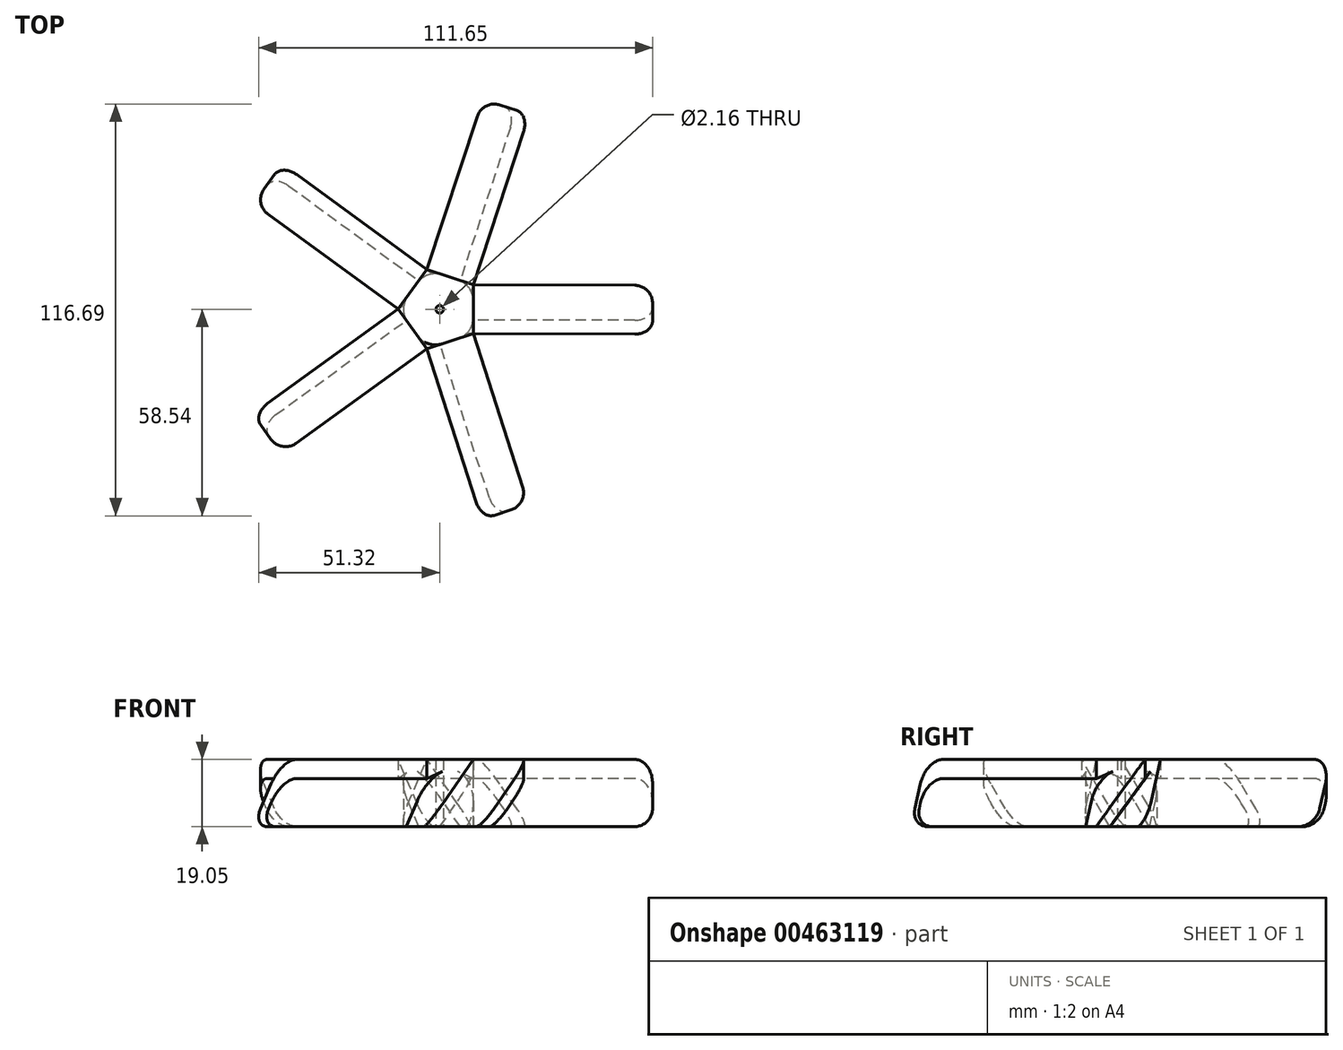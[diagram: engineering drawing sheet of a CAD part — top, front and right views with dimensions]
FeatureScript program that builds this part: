
annotation { "Feature Type Name" : "Feature", "Feature Type Description" : "" }
export const myFeature = defineFeature(function(context is Context, id is Id, definition is map)
    precondition{}
    {
        {
            var Q0;
            Q0=qCreatedBy(makeId("Top.planeOp"),FACE);
            var sketch = newSketch(context, id + "F0", { "sketchPlane" : qUnion([Q0])});
            skCircle(sketch, "E0.cCircle", {"center": v(0, 0) * mm, "radius": 9.53 * mm, "construction": true});
            skLineSegment(sketch, "E0.0", {"start": v(9.5, -6.94) * mm, "end": v(-3.67, -11.19) * mm});
            skLineSegment(sketch, "E0.1", {"start": v(-3.67, -11.19) * mm, "end": v(-11.77, 0.03) * mm});
            skLineSegment(sketch, "E0.2", {"start": v(-11.77, 0.03) * mm, "end": v(-3.61, 11.2) * mm});
            skLineSegment(sketch, "E0.3", {"start": v(-3.61, 11.2) * mm, "end": v(9.54, 6.9) * mm});
            skLineSegment(sketch, "E0.4", {"start": v(9.54, 6.9) * mm, "end": v(9.5, -6.94) * mm});
            skPoint(sketch, "E0.0.midPoint", {"position": v(2.92, -9.07) * mm});
            skCircle(sketch, "E1", {"center": v(0, 0) * mm, "radius": 1.08 * mm});
            skSolve(sketch);
        }
        {
            var Q0;
            Q0=makeQuery(id+"F0.imprint","IMPRINT",FACE,{"disambiguationData":[TD([[makeQuery(id+"F0.imprint","IMPRINT",EDGE,{"derivedFrom":sQuery(id+"F0.wireOp",EDGE,"E0.0")}),-1.0]])]});
            extrude(context, id + "F1", {"entities" : qUnion([Q0]), "depth" : 19.05 * mm});
        }
        {
            var Q0;
            Q0=makeQuery(id+"F1.opExtrude","SWEPT_FACE",FACE,{"disambiguationData":[OSD([sQuery(id+"F0.wireOp",EDGE,"E0.1")])]});
            var sketch = newSketch(context, id + "F2", { "sketchPlane" : qUnion([Q0])});
            skLineSegment(sketch, "E2", {"start": v(-6.92, 0) * mm, "end": v(6.92, 19.05) * mm});
            skLineSegment(sketch, "E3.0", {"start": v(-6.66, -5.04) * mm, "end": v(11.8, 20.36) * mm});
            skSolve(sketch);
        }
        {
            var Q0;
            {var subQ0=sQuery(id+"F2.wireOp",EDGE,"E2");Q0=makeQuery(id+"F2.imprint","IMPRINT",FACE,{"disambiguationData":[TD([[makeQuery(id+"F2.imprint","IMPRINT",EDGE,{"derivedFrom":subQ0}),-1.0]])]});}
            extrude(context, id + "F3", {"entities" : qUnion([Q0]), "operationType" : NewBodyOperationType.ADD, "depth" : 50.8 * mm});
        }
        {
            var Q0;
            Q0=makeQuery(id+"F1.opExtrude","SWEPT_FACE",FACE,{"disambiguationData":[OSD([sQuery(id+"F0.wireOp",EDGE,"E0.0")])]});
            var sketch = newSketch(context, id + "F4", { "sketchPlane" : qUnion([Q0])});
            skLineSegment(sketch, "E4", {"start": v(-6.92, 0) * mm, "end": v(6.92, 19.05) * mm});
            skLineSegment(sketch, "E5.0", {"start": v(-6.66, -5.04) * mm, "end": v(11.8, 20.36) * mm});
            skSolve(sketch);
        }
        {
            var Q0;
            {var subQ0=sQuery(id+"F4.wireOp",EDGE,"E4");Q0=makeQuery(id+"F4.imprint","IMPRINT",FACE,{"disambiguationData":[TD([[makeQuery(id+"F4.imprint","IMPRINT",EDGE,{"derivedFrom":subQ0}),-1.0]])]});}
            extrude(context, id + "F5", {"entities" : qUnion([Q0]), "operationType" : NewBodyOperationType.ADD, "depth" : 50.8 * mm});
        }
        {
            var Q0;
            Q0=makeQuery(id+"F1.opExtrude","SWEPT_FACE",FACE,{"disambiguationData":[OSD([sQuery(id+"F0.wireOp",EDGE,"E0.4")])]});
            var sketch = newSketch(context, id + "F6", { "sketchPlane" : qUnion([Q0])});
            skLineSegment(sketch, "E6", {"start": v(-6.92, 0) * mm, "end": v(6.92, 19.05) * mm});
            skLineSegment(sketch, "E7.0", {"start": v(-6.66, -5.04) * mm, "end": v(11.8, 20.36) * mm});
            skSolve(sketch);
        }
        {
            var Q0;
            {var subQ0=sQuery(id+"F6.wireOp",EDGE,"E6");Q0=makeQuery(id+"F6.imprint","IMPRINT",FACE,{"disambiguationData":[TD([[makeQuery(id+"F6.imprint","IMPRINT",EDGE,{"derivedFrom":subQ0}),-1.0]])]});}
            extrude(context, id + "F7", {"entities" : qUnion([Q0]), "operationType" : NewBodyOperationType.ADD, "depth" : 50.8 * mm});
        }
        {
            var Q0;
            Q0=makeQuery(id+"F1.opExtrude","SWEPT_FACE",FACE,{"disambiguationData":[OSD([sQuery(id+"F0.wireOp",EDGE,"E0.3")])]});
            var sketch = newSketch(context, id + "F8", { "sketchPlane" : qUnion([Q0])});
            skLineSegment(sketch, "E8", {"start": v(-6.92, 0) * mm, "end": v(6.92, 19.05) * mm});
            skLineSegment(sketch, "E9.0", {"start": v(-6.66, -5.04) * mm, "end": v(11.8, 20.36) * mm});
            skSolve(sketch);
        }
        {
            var Q0;
            {var subQ0=sQuery(id+"F8.wireOp",EDGE,"E8");Q0=makeQuery(id+"F8.imprint","IMPRINT",FACE,{"disambiguationData":[TD([[makeQuery(id+"F8.imprint","IMPRINT",EDGE,{"derivedFrom":subQ0}),-1.0]])]});}
            extrude(context, id + "F9", {"entities" : qUnion([Q0]), "operationType" : NewBodyOperationType.ADD, "depth" : 50.8 * mm});
        }
        {
            var Q0;
            Q0=makeQuery(id+"F1.opExtrude","SWEPT_FACE",FACE,{"disambiguationData":[OSD([sQuery(id+"F0.wireOp",EDGE,"E0.2")])]});
            var sketch = newSketch(context, id + "F10", { "sketchPlane" : qUnion([Q0])});
            skLineSegment(sketch, "E10", {"start": v(-6.92, 0) * mm, "end": v(6.92, 19.05) * mm});
            skLineSegment(sketch, "E11.0", {"start": v(-6.66, -5.04) * mm, "end": v(11.8, 20.36) * mm});
            skSolve(sketch);
        }
        {
            var Q0;
            {var subQ0=sQuery(id+"F10.wireOp",EDGE,"E10");Q0=makeQuery(id+"F10.imprint","IMPRINT",FACE,{"disambiguationData":[TD([[makeQuery(id+"F10.imprint","IMPRINT",EDGE,{"derivedFrom":subQ0}),-1.0]])]});}
            extrude(context, id + "F11", {"entities" : qUnion([Q0]), "operationType" : NewBodyOperationType.ADD, "depth" : 50.8 * mm});
        }
        {
            var Q0;
            Q0=makeQuery(id+"F9.boolean.opBoolean","SPLIT",EDGE,{"derivedFrom":makeQuery(id+"F1.opExtrude","SWEPT_EDGE",EDGE,{"disambiguationData":[OSD([sQuery(id+"F0.wireOp",EDGE,"E0.2"),sQuery(id+"F0.wireOp",EDGE,"E0.3")])]})});
            var Q1;
            Q1=makeQuery(id+"F11.boolean.opBoolean","SPLIT",EDGE,{"derivedFrom":makeQuery(id+"F1.opExtrude","SWEPT_EDGE",EDGE,{"disambiguationData":[OSD([sQuery(id+"F0.wireOp",EDGE,"E0.1"),sQuery(id+"F0.wireOp",EDGE,"E0.2")])]})});
            var Q2;
            Q2=makeQuery(id+"F3.boolean.opBoolean","SPLIT",EDGE,{"derivedFrom":makeQuery(id+"F1.opExtrude","SWEPT_EDGE",EDGE,{"disambiguationData":[OSD([sQuery(id+"F0.wireOp",EDGE,"E0.0"),sQuery(id+"F0.wireOp",EDGE,"E0.1")])]})});
            var Q3;
            Q3=makeQuery(id+"F5.boolean.opBoolean","SPLIT",EDGE,{"derivedFrom":makeQuery(id+"F1.opExtrude","SWEPT_EDGE",EDGE,{"disambiguationData":[OSD([sQuery(id+"F0.wireOp",EDGE,"E0.0"),sQuery(id+"F0.wireOp",EDGE,"E0.4")])]})});
            var Q4;
            Q4=makeQuery(id+"F7.boolean.opBoolean","SPLIT",EDGE,{"derivedFrom":makeQuery(id+"F1.opExtrude","SWEPT_EDGE",EDGE,{"disambiguationData":[OSD([sQuery(id+"F0.wireOp",EDGE,"E0.3"),sQuery(id+"F0.wireOp",EDGE,"E0.4")])]})});
            fillet(context, id + "F12", {"entities" : qUnion([Q0, Q1, Q2, Q3, Q4]), "radius" : 6.35 * mm, "tangentPropagation" : true, "allowEdgeOverflow" : false});
        }
        {
            var Q0;
            Q0=makeQuery(id+"F11.opExtrude","CAP_EDGE",EDGE,{"disambiguationData":[OSD([sQuery(id+"F0.wireOp",EDGE,"E0.1"),sQuery(id+"F0.wireOp",EDGE,"E0.2")])],"isStart":false});
            var Q1;
            Q1=makeQuery(id+"F11.opExtrude","CAP_EDGE",EDGE,{"disambiguationData":[OSD([sQuery(id+"F0.wireOp",EDGE,"E0.2")])],"isStart":false});
            var Q2;
            Q2=makeQuery(id+"F3.opExtrude","CAP_EDGE",EDGE,{"disambiguationData":[OSD([sQuery(id+"F0.wireOp",EDGE,"E0.1")])],"isStart":false});
            var Q3;
            Q3=makeQuery(id+"F3.opExtrude","CAP_EDGE",EDGE,{"disambiguationData":[OSD([sQuery(id+"F0.wireOp",EDGE,"E0.0"),sQuery(id+"F0.wireOp",EDGE,"E0.1")])],"isStart":false});
            var Q4;
            Q4=makeQuery(id+"F5.opExtrude","CAP_EDGE",EDGE,{"disambiguationData":[OSD([sQuery(id+"F0.wireOp",EDGE,"E0.0")])],"isStart":false});
            var Q5;
            Q5=makeQuery(id+"F5.opExtrude","CAP_EDGE",EDGE,{"disambiguationData":[OSD([sQuery(id+"F0.wireOp",EDGE,"E0.0"),sQuery(id+"F0.wireOp",EDGE,"E0.4")])],"isStart":false});
            var Q6;
            Q6=makeQuery(id+"F7.opExtrude","CAP_EDGE",EDGE,{"disambiguationData":[OSD([sQuery(id+"F0.wireOp",EDGE,"E0.4")])],"isStart":false});
            var Q7;
            Q7=makeQuery(id+"F7.opExtrude","CAP_EDGE",EDGE,{"disambiguationData":[OSD([sQuery(id+"F0.wireOp",EDGE,"E0.3"),sQuery(id+"F0.wireOp",EDGE,"E0.4")])],"isStart":false});
            var Q8;
            Q8=makeQuery(id+"F9.opExtrude","CAP_EDGE",EDGE,{"disambiguationData":[OSD([sQuery(id+"F0.wireOp",EDGE,"E0.3")])],"isStart":false});
            var Q9;
            Q9=makeQuery(id+"F9.opExtrude","CAP_EDGE",EDGE,{"disambiguationData":[OSD([sQuery(id+"F0.wireOp",EDGE,"E0.2"),sQuery(id+"F0.wireOp",EDGE,"E0.3")])],"isStart":false});
            fillet(context, id + "F13", {"entities" : qUnion([Q0, Q1, Q2, Q3, Q4, Q5, Q6, Q7, Q8, Q9]), "radius" : 5.08 * mm, "tangentPropagation" : true, "allowEdgeOverflow" : false});
        }
    });
